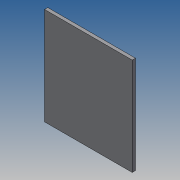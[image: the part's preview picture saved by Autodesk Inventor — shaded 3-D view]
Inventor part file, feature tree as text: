
AUTODESK INVENTOR PART (.ipt)
format: ipt  version: 2017 (Build 210142000, 142)  size: 206,336 bytes
history: native  units: mm
features: reference x12, other x5, extrude x4, sketch x4, projected_geometry x1
ambient origin geometry x8: Origin, YZ Plane, XZ Plane, XY Plane, X Axis, Y Axis, Z Axis, Center Point
bodies: Body1 (feature_tree)
feature tree (26):
  other  "Sólido1"
  extrude  "Extrusión1"  Depth=120.0mm
  sketch  "Boceto2"  dims[d6=4.0mm d7=0.0mm d9=27.0mm]
  extrude  "Extrusión2"  Depth=4.0mm
  extrude  "Extrusión3"  Depth=10.0mm
  extrude  "Extrusión4"  Depth=12.0mm
  sketch  "Boceto1"  dims[d0=108.0mm d1=120.0mm]
  reference  "Referencia1"
  reference  "Referencia2"
  reference  "Referencia3"
  reference  "Referencia4"
  reference  "Referencia5"
  reference  "Referencia6"
  reference  "Referencia7"
  reference  "Referencia8"
  sketch  "Boceto3"  dims[d10=3.0mm d11=10.0mm]
  projected_geometry  "Contorno proyectado1"
  sketch  "Boceto4"  dims[d12=12.0mm d13=12.0mm d14=12.0mm d15=45.0deg d16=8.0mm d17=8.0mm d18=8.0mm d19=8.0mm d20=8.0mm d21=8.0mm d22=8.0mm d23=8.0mm d24=8.0mm d25=8.0mm d26=8.0mm d27=8.0mm d28=8.0mm d29=8.0mm d30=8.0mm d31=10.0mm d32=0.0mm d33=16.0mm d34=4.0mm d35=0.0mm d36=10.0mm d37=0.0mm]
  reference  "Referencia9"
  reference  "Referencia10"
  reference  "Referencia11"
  reference  "Referencia12"
  other  "<userpath>\Documents\GitHub\actor-re-actor\models\inventor-caja\Piezas\componentes.iam"
  other  "componentes.iam"
  other  "driver motor:1"
  other  "dimmer:1"
